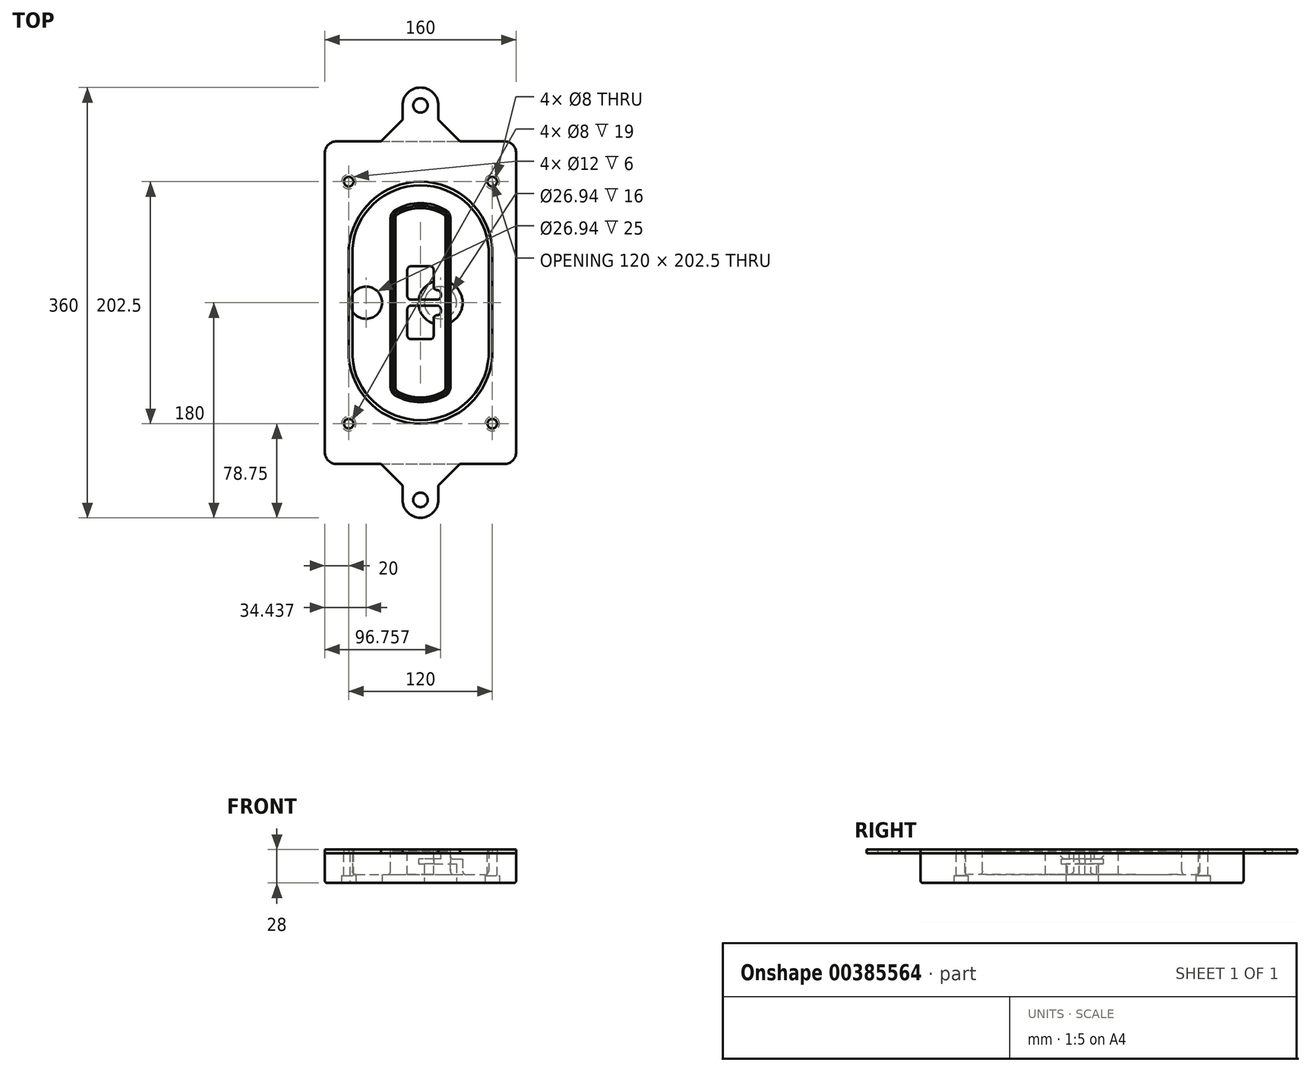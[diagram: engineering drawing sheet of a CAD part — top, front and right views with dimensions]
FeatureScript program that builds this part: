
annotation { "Feature Type Name" : "Feature", "Feature Type Description" : "" }
export const myFeature = defineFeature(function(context is Context, id is Id, definition is map)
    precondition{}
    {
        {
            var Q0;
            Q0=qCreatedBy(makeId("Top.planeOp"),FACE);
            var sketch = newSketch(context, id + "F0", { "sketchPlane" : qUnion([Q0])});
            skPoint(sketch, "E0.rect.middle", {"position": v(0, 0) * mm});
            skLineSegment(sketch, "E1.bottom", {"start": v(-70, -135) * mm, "end": v(70, -135) * mm});
            skLineSegment(sketch, "E1.top", {"start": v(-70, 135) * mm, "end": v(70, 135) * mm});
            skLineSegment(sketch, "E1.left", {"start": v(-80, -125) * mm, "end": v(-80, 125) * mm});
            skLineSegment(sketch, "E1.right", {"start": v(80, -125) * mm, "end": v(80, 125) * mm});
            skLineSegment(sketch, "E2", {"start": v(-80, 135) * mm, "end": v(80, -135) * mm, "construction": true});
            skLineSegment(sketch, "E3", {"start": v(80, 135) * mm, "end": v(-80, -135) * mm, "construction": true});
            skCircle(sketch, "E4", {"center": v(-60, 101.25) * mm, "radius": 4 * mm});
            skCircle(sketch, "E5", {"center": v(60, 101.25) * mm, "radius": 4 * mm});
            skCircle(sketch, "E6", {"center": v(60, -101.25) * mm, "radius": 4 * mm});
            skCircle(sketch, "E7", {"center": v(-60, -101.25) * mm, "radius": 4 * mm});
            skLineSegment(sketch, "E8", {"start": v(-60, 101.25) * mm, "end": v(60, 101.25) * mm, "construction": true});
            skLineSegment(sketch, "E9", {"start": v(60, 101.25) * mm, "end": v(60, -101.25) * mm, "construction": true});
            skLineSegment(sketch, "E10", {"start": v(60, -101.25) * mm, "end": v(-60, -101.25) * mm, "construction": true});
            skLineSegment(sketch, "E11", {"start": v(-60, -101.25) * mm, "end": v(-60, 101.25) * mm, "construction": true});
            skLineSegment(sketch, "E12", {"start": v(-60, 44.66) * mm, "end": v(-60, -44.66) * mm});
            skLineSegment(sketch, "E13", {"start": v(60, 44.66) * mm, "end": v(60, -44.66) * mm});
            skArc(sketch, "E14", {"start": v(59.98, 45.37) * mm, "mid": v(0, 101.25) * mm, "end": v(-59.98, 45.37) * mm});
            skArc(sketch, "E15", {"start": v(-59.98, -45.37) * mm, "mid": v(0, -101.25) * mm, "end": v(59.98, -45.37) * mm});
            skLineSegment(sketch, "E16", {"start": v(-60, 0) * mm, "end": v(60, 0) * mm, "construction": true});
            skPoint(sketch, "E17.visualSharp", {"position": v(-60, -45) * mm});
            skArc(sketch, "E17.filletArc", {"start": v(-60, -44.66) * mm, "mid": v(-60, -45.02) * mm, "end": v(-59.98, -45.37) * mm});
            skPoint(sketch, "E18.visualSharp", {"position": v(-60, 45) * mm});
            skArc(sketch, "E18.filletArc", {"start": v(-59.98, 45.37) * mm, "mid": v(-60, 45.02) * mm, "end": v(-60, 44.66) * mm});
            skPoint(sketch, "E19.visualSharp", {"position": v(60, 45) * mm});
            skArc(sketch, "E19.filletArc", {"start": v(60, 44.66) * mm, "mid": v(60, 45.02) * mm, "end": v(59.98, 45.37) * mm});
            skPoint(sketch, "E20.visualSharp", {"position": v(60, -45) * mm});
            skArc(sketch, "E20.filletArc", {"start": v(59.98, -45.37) * mm, "mid": v(60, -45.02) * mm, "end": v(60, -44.66) * mm});
            skPoint(sketch, "E21.visualSharp", {"position": v(-80, 135) * mm});
            skArc(sketch, "E21.filletArc", {"start": v(-70, 135) * mm, "mid": v(-77.07, 132.07) * mm, "end": v(-80, 125) * mm});
            skPoint(sketch, "E22.visualSharp", {"position": v(80, 135) * mm});
            skArc(sketch, "E22.filletArc", {"start": v(80, 125) * mm, "mid": v(77.07, 132.07) * mm, "end": v(70, 135) * mm});
            skPoint(sketch, "E23.visualSharp", {"position": v(80, -135) * mm});
            skArc(sketch, "E23.filletArc", {"start": v(70, -135) * mm, "mid": v(77.07, -132.07) * mm, "end": v(80, -125) * mm});
            skPoint(sketch, "E24.visualSharp", {"position": v(-80, -135) * mm});
            skArc(sketch, "E24.filletArc", {"start": v(-80, -125) * mm, "mid": v(-77.07, -132.07) * mm, "end": v(-70, -135) * mm});
            skArc(sketch, "E25.0", {"start": v(57, 44.66) * mm, "mid": v(57, 44.9) * mm, "end": v(56.98, 45.16) * mm});
            skLineSegment(sketch, "E25.1", {"start": v(57, 44.66) * mm, "end": v(57, -44.66) * mm});
            skArc(sketch, "E25.2", {"start": v(56.98, -45.16) * mm, "mid": v(57, -44.9) * mm, "end": v(57, -44.66) * mm});
            skArc(sketch, "E25.3", {"start": v(-56.98, -45.16) * mm, "mid": v(0, -98.25) * mm, "end": v(56.98, -45.16) * mm});
            skArc(sketch, "E25.4", {"start": v(-57, -44.66) * mm, "mid": v(-57, -44.9) * mm, "end": v(-56.98, -45.16) * mm});
            skArc(sketch, "E25.5", {"start": v(56.98, 45.16) * mm, "mid": v(0, 98.25) * mm, "end": v(-56.98, 45.16) * mm});
            skLineSegment(sketch, "E25.6", {"start": v(-57, 44.66) * mm, "end": v(-57, -44.66) * mm});
            skArc(sketch, "E25.7", {"start": v(-56.98, 45.16) * mm, "mid": v(-57, 44.9) * mm, "end": v(-57, 44.66) * mm});
            skArc(sketch, "E26.0", {"start": v(-63.97, 45.65) * mm, "mid": v(-64, 45.16) * mm, "end": v(-64, 44.66) * mm});
            skArc(sketch, "E26.1", {"start": v(63.97, 45.65) * mm, "mid": v(0, 105.25) * mm, "end": v(-63.97, 45.65) * mm});
            skArc(sketch, "E26.2", {"start": v(64, 44.66) * mm, "mid": v(64, 45.16) * mm, "end": v(63.97, 45.65) * mm});
            skLineSegment(sketch, "E26.3", {"start": v(64, 44.66) * mm, "end": v(64, -44.66) * mm});
            skArc(sketch, "E26.4", {"start": v(63.97, -45.65) * mm, "mid": v(64, -45.16) * mm, "end": v(64, -44.66) * mm});
            skLineSegment(sketch, "E26.5", {"start": v(-64, 44.66) * mm, "end": v(-64, -44.66) * mm});
            skArc(sketch, "E26.6", {"start": v(-63.97, -45.65) * mm, "mid": v(0, -105.25) * mm, "end": v(63.97, -45.65) * mm});
            skArc(sketch, "E26.7", {"start": v(-64, -44.66) * mm, "mid": v(-64, -45.16) * mm, "end": v(-63.97, -45.65) * mm});
            skSolve(sketch);
        }
        {
            var Q0;
            Q0=makeQuery(id+"F0.imprint","IMPRINT",FACE,{"disambiguationData":[TD([[makeQuery(id+"F0.imprint","IMPRINT",EDGE,{"derivedFrom":sQuery(id+"F0.wireOp",EDGE,"E1.bottom")}),1.0]])]});
            var Q1;
            Q1=makeQuery(id+"F0.imprint","IMPRINT",FACE,{"disambiguationData":[TD([[makeQuery(id+"F0.imprint","IMPRINT",EDGE,{"derivedFrom":sQuery(id+"F0.wireOp",EDGE,"E12")}),1.0]])]});
            var Q2;
            Q2=makeQuery(id+"F0.imprint","IMPRINT",FACE,{"disambiguationData":[TD([[makeQuery(id+"F0.imprint","IMPRINT",EDGE,{"derivedFrom":sQuery(id+"F0.wireOp",EDGE,"E25.0")}),1.0]])]});
            var Q3;
            Q3=makeQuery(id+"F0.imprint","IMPRINT",FACE,{"disambiguationData":[TD([[makeQuery(id+"F0.imprint","IMPRINT",EDGE,{"derivedFrom":sQuery(id+"F0.wireOp",EDGE,"E12")}),-1.0]])]});
            extrude(context, id + "F1", {"entities" : qUnion([Q0, Q1, Q2, Q3]), "oppositeDirection" : true, "depth" : 25 * mm});
        }
        {
            var Q0;
            Q0=makeQuery(id+"F0.imprint","IMPRINT",FACE,{"disambiguationData":[TD([[makeQuery(id+"F0.imprint","IMPRINT",EDGE,{"derivedFrom":sQuery(id+"F0.wireOp",EDGE,"E12")}),1.0]])]});
            extrude(context, id + "F2", {"entities" : qUnion([Q0]), "operationType" : NewBodyOperationType.ADD, "depth" : 3 * mm});
        }
        {
            var Q0;
            Q0=makeQuery(id+"F0.imprint","IMPRINT",FACE,{"disambiguationData":[TD([[makeQuery(id+"F0.imprint","IMPRINT",EDGE,{"derivedFrom":sQuery(id+"F0.wireOp",EDGE,"E25.0")}),1.0]])]});
            extrude(context, id + "F3", {"entities" : qUnion([Q0]), "operationType" : NewBodyOperationType.REMOVE, "oppositeDirection" : true, "depth" : 18 * mm});
        }
        {
            var Q0;
            Q0=makeQuery(id+"F2.opExtrude","CAP_FACE",FACE,{"disambiguationData":[OSD([sQuery(id+"F0.wireOp",EDGE,"E12"),sQuery(id+"F0.wireOp",EDGE,"E13"),sQuery(id+"F0.wireOp",EDGE,"E14"),sQuery(id+"F0.wireOp",EDGE,"E15"),sQuery(id+"F0.wireOp",EDGE,"E17.filletArc"),sQuery(id+"F0.wireOp",EDGE,"E18.filletArc"),sQuery(id+"F0.wireOp",EDGE,"E19.filletArc"),sQuery(id+"F0.wireOp",EDGE,"E20.filletArc"),sQuery(id+"F0.wireOp",EDGE,"E25.0"),sQuery(id+"F0.wireOp",EDGE,"E25.1"),sQuery(id+"F0.wireOp",EDGE,"E25.2"),sQuery(id+"F0.wireOp",EDGE,"E25.3"),sQuery(id+"F0.wireOp",EDGE,"E25.4"),sQuery(id+"F0.wireOp",EDGE,"E25.5"),sQuery(id+"F0.wireOp",EDGE,"E25.6"),sQuery(id+"F0.wireOp",EDGE,"E25.7")])],"isStart":false});
            var sketch = newSketch(context, id + "F4", { "sketchPlane" : qUnion([Q0])});
            skArc(sketch, "E27.0", {"start": v(-20.99, -77.65) * mm, "mid": v(0, -83.25) * mm, "end": v(20.99, -77.65) * mm});
            skArc(sketch, "E28.0", {"start": v(20.99, 77.65) * mm, "mid": v(0, 83.25) * mm, "end": v(-20.99, 77.65) * mm});
            skLineSegment(sketch, "E29", {"start": v(-25, 70.71) * mm, "end": v(-25, -70.71) * mm});
            skLineSegment(sketch, "E30", {"start": v(25, 70.71) * mm, "end": v(25, -70.71) * mm});
            skLineSegment(sketch, "E31", {"start": v(-25, 75.03) * mm, "end": v(25, 75.03) * mm, "construction": true});
            skLineSegment(sketch, "E32", {"start": v(-25, -75.03) * mm, "end": v(25, -75.03) * mm, "construction": true});
            skPoint(sketch, "E33.visualSharp", {"position": v(-25, 75.03) * mm});
            skArc(sketch, "E33.filletArc", {"start": v(-20.99, 77.65) * mm, "mid": v(-23.92, 74.72) * mm, "end": v(-25, 70.71) * mm});
            skPoint(sketch, "E34.visualSharp", {"position": v(25, 75.03) * mm});
            skArc(sketch, "E34.filletArc", {"start": v(25, 70.71) * mm, "mid": v(23.92, 74.72) * mm, "end": v(20.99, 77.65) * mm});
            skPoint(sketch, "E35.visualSharp", {"position": v(25, -75.03) * mm});
            skArc(sketch, "E35.filletArc", {"start": v(20.99, -77.65) * mm, "mid": v(23.92, -74.72) * mm, "end": v(25, -70.71) * mm});
            skPoint(sketch, "E36.visualSharp", {"position": v(-25, -75.03) * mm});
            skArc(sketch, "E36.filletArc", {"start": v(-25, -70.71) * mm, "mid": v(-23.92, -74.72) * mm, "end": v(-20.99, -77.65) * mm});
            skArc(sketch, "E37.0", {"start": v(56.98, 45.16) * mm, "mid": v(0, 98.25) * mm, "end": v(-56.98, 45.16) * mm});
            skArc(sketch, "E37.1", {"start": v(-56.98, 45.16) * mm, "mid": v(-57, 44.9) * mm, "end": v(-57, 44.66) * mm});
            skLineSegment(sketch, "E37.2", {"start": v(-57, 44.66) * mm, "end": v(-57, -44.66) * mm});
            skArc(sketch, "E37.3", {"start": v(-57, -44.66) * mm, "mid": v(-57, -44.9) * mm, "end": v(-56.98, -45.16) * mm});
            skArc(sketch, "E37.4", {"start": v(-56.98, -45.16) * mm, "mid": v(0, -98.25) * mm, "end": v(56.98, -45.16) * mm});
            skArc(sketch, "E37.5", {"start": v(56.98, -45.16) * mm, "mid": v(57, -44.9) * mm, "end": v(57, -44.66) * mm});
            skLineSegment(sketch, "E37.6", {"start": v(57, 44.66) * mm, "end": v(57, -44.66) * mm});
            skArc(sketch, "E37.7", {"start": v(57, 44.66) * mm, "mid": v(57, 44.9) * mm, "end": v(56.98, 45.16) * mm});
            skLineSegment(sketch, "E38.0", {"start": v(23, 70.71) * mm, "end": v(23, -70.71) * mm});
            skArc(sketch, "E38.1", {"start": v(19.99, -75.92) * mm, "mid": v(22.2, -73.72) * mm, "end": v(23, -70.71) * mm});
            skArc(sketch, "E38.2", {"start": v(-19.99, -75.92) * mm, "mid": v(0, -81.25) * mm, "end": v(19.99, -75.92) * mm});
            skArc(sketch, "E38.3", {"start": v(-23, -70.71) * mm, "mid": v(-22.2, -73.72) * mm, "end": v(-19.99, -75.92) * mm});
            skLineSegment(sketch, "E38.4", {"start": v(-23, 70.71) * mm, "end": v(-23, -70.71) * mm});
            skArc(sketch, "E38.5", {"start": v(23, 70.71) * mm, "mid": v(22.2, 73.72) * mm, "end": v(19.99, 75.92) * mm});
            skArc(sketch, "E38.6", {"start": v(-19.99, 75.92) * mm, "mid": v(-22.2, 73.72) * mm, "end": v(-23, 70.71) * mm});
            skArc(sketch, "E38.7", {"start": v(19.99, 75.92) * mm, "mid": v(0, 81.25) * mm, "end": v(-19.99, 75.92) * mm});
            skArc(sketch, "E39.0", {"start": v(21, 70.71) * mm, "mid": v(20.46, 72.72) * mm, "end": v(19, 74.18) * mm});
            skLineSegment(sketch, "E39.1", {"start": v(21, 70.71) * mm, "end": v(21, -70.71) * mm});
            skArc(sketch, "E39.2", {"start": v(19, -74.18) * mm, "mid": v(20.46, -72.72) * mm, "end": v(21, -70.71) * mm});
            skArc(sketch, "E39.3", {"start": v(-19, -74.18) * mm, "mid": v(0, -79.25) * mm, "end": v(19, -74.18) * mm});
            skArc(sketch, "E39.4", {"start": v(-21, -70.71) * mm, "mid": v(-20.46, -72.72) * mm, "end": v(-19, -74.18) * mm});
            skArc(sketch, "E39.5", {"start": v(19, 74.18) * mm, "mid": v(0, 79.25) * mm, "end": v(-19, 74.18) * mm});
            skLineSegment(sketch, "E39.6", {"start": v(-21, 70.71) * mm, "end": v(-21, -70.71) * mm});
            skArc(sketch, "E39.7", {"start": v(-19, 74.18) * mm, "mid": v(-20.46, 72.72) * mm, "end": v(-21, 70.71) * mm});
            skLineSegment(sketch, "E40", {"start": v(-25, 0) * mm, "end": v(25, 0) * mm, "construction": true});
            skLineSegment(sketch, "E41", {"start": v(-11, 5.5) * mm, "end": v(-11, 27.5) * mm});
            skLineSegment(sketch, "E42", {"start": v(-8, 30.5) * mm, "end": v(8, 30.5) * mm});
            skLineSegment(sketch, "E43", {"start": v(11, 27.5) * mm, "end": v(11, 13.5) * mm});
            skLineSegment(sketch, "E44", {"start": v(14, 10.5) * mm, "end": v(14, 10.5) * mm});
            skLineSegment(sketch, "E45", {"start": v(17, 7.5) * mm, "end": v(17, 5.5) * mm});
            skLineSegment(sketch, "E46", {"start": v(14, 2.5) * mm, "end": v(-8, 2.5) * mm});
            skPoint(sketch, "E47.visualSharp", {"position": v(-11, 30.5) * mm});
            skArc(sketch, "E47.filletArc", {"start": v(-8, 30.5) * mm, "mid": v(-10.12, 29.62) * mm, "end": v(-11, 27.5) * mm});
            skPoint(sketch, "E48.visualSharp", {"position": v(11, 30.5) * mm});
            skArc(sketch, "E48.filletArc", {"start": v(11, 27.5) * mm, "mid": v(10.12, 29.62) * mm, "end": v(8, 30.5) * mm});
            skPoint(sketch, "E49.visualSharp", {"position": v(11, 10.5) * mm});
            skArc(sketch, "E49.filletArc", {"start": v(11, 13.5) * mm, "mid": v(11.88, 11.38) * mm, "end": v(14, 10.5) * mm});
            skPoint(sketch, "E50.visualSharp", {"position": v(17, 10.5) * mm});
            skArc(sketch, "E50.filletArc", {"start": v(17, 7.5) * mm, "mid": v(16.12, 9.62) * mm, "end": v(14, 10.5) * mm});
            skPoint(sketch, "E51.visualSharp", {"position": v(17, 2.5) * mm});
            skArc(sketch, "E51.filletArc", {"start": v(14, 2.5) * mm, "mid": v(16.12, 3.38) * mm, "end": v(17, 5.5) * mm});
            skPoint(sketch, "E52.visualSharp", {"position": v(-11, 2.5) * mm});
            skArc(sketch, "E52.filletArc", {"start": v(-11, 5.5) * mm, "mid": v(-10.12, 3.38) * mm, "end": v(-8, 2.5) * mm});
            skLineSegment(sketch, "E53.0.MirrorCS", {"start": v(14, -2.5) * mm, "end": v(-8, -2.5) * mm});
            skArc(sketch, "E54.0.MirrorCS", {"start": v(-11, -5.5) * mm, "mid": v(-10.12, -3.38) * mm, "end": v(-8, -2.5) * mm});
            skLineSegment(sketch, "E55.0.MirrorCS", {"start": v(-11, -5.5) * mm, "end": v(-11, -27.5) * mm});
            skArc(sketch, "E56.0.MirrorCS", {"start": v(-8, -30.5) * mm, "mid": v(-10.12, -29.62) * mm, "end": v(-11, -27.5) * mm});
            skLineSegment(sketch, "E57.0.MirrorCS", {"start": v(-8, -30.5) * mm, "end": v(8, -30.5) * mm});
            skArc(sketch, "E58.0.MirrorCS", {"start": v(11, -27.5) * mm, "mid": v(10.12, -29.62) * mm, "end": v(8, -30.5) * mm});
            skLineSegment(sketch, "E59.0.MirrorCS", {"start": v(11, -27.5) * mm, "end": v(11, -13.5) * mm});
            skArc(sketch, "E60.0.MirrorCS", {"start": v(11, -13.5) * mm, "mid": v(11.88, -11.38) * mm, "end": v(14, -10.5) * mm});
            skArc(sketch, "E61.0.MirrorCS", {"start": v(17, -7.5) * mm, "mid": v(16.12, -9.62) * mm, "end": v(14, -10.5) * mm});
            skLineSegment(sketch, "E62.0.MirrorCS", {"start": v(17, -7.5) * mm, "end": v(17, -5.5) * mm});
            skArc(sketch, "E63.0.MirrorCS", {"start": v(14, -2.5) * mm, "mid": v(16.12, -3.38) * mm, "end": v(17, -5.5) * mm});
            skSolve(sketch);
        }
        {
            var Q0;
            Q0=makeQuery(id+"F4.imprint","IMPRINT",FACE,{"disambiguationData":[TD([[makeQuery(id+"F4.imprint","IMPRINT",EDGE,{"derivedFrom":sQuery(id+"F4.wireOp",EDGE,"E27.0")}),1.0]])]});
            var Q1;
            Q1=makeQuery(id+"F4.imprint","IMPRINT",FACE,{"disambiguationData":[TD([[makeQuery(id+"F4.imprint","IMPRINT",EDGE,{"derivedFrom":sQuery(id+"F4.wireOp",EDGE,"E38.0")}),-1.0]])]});
            var Q2;
            Q2=makeQuery(id+"F4.imprint","IMPRINT",FACE,{"disambiguationData":[TD([[makeQuery(id+"F4.imprint","IMPRINT",EDGE,{"derivedFrom":sQuery(id+"F4.wireOp",EDGE,"E39.0")}),1.0]])]});
            extrude(context, id + "F5", {"entities" : qUnion([Q0, Q1, Q2]), "operationType" : NewBodyOperationType.ADD, "endBound" : BoundingType.UP_TO_NEXT, "oppositeDirection" : true, "depth" : 25 * mm});
        }
        {
            var Q0;
            Q0=makeQuery(id+"F4.imprint","IMPRINT",FACE,{"disambiguationData":[TD([[makeQuery(id+"F4.imprint","IMPRINT",EDGE,{"derivedFrom":sQuery(id+"F4.wireOp",EDGE,"E38.0")}),-1.0]])]});
            extrude(context, id + "F6", {"entities" : qUnion([Q0]), "operationType" : NewBodyOperationType.REMOVE, "oppositeDirection" : true, "depth" : 2 * mm});
        }
        {
            var Q0;
            Q0=makeQuery(id+"F1.opExtrude","CAP_FACE",FACE,{"disambiguationData":[OSD([sQuery(id+"F0.wireOp",EDGE,"E1.bottom"),sQuery(id+"F0.wireOp",EDGE,"E1.top"),sQuery(id+"F0.wireOp",EDGE,"E1.left"),sQuery(id+"F0.wireOp",EDGE,"E1.right"),sQuery(id+"F0.wireOp",EDGE,"E4"),sQuery(id+"F0.wireOp",EDGE,"E5"),sQuery(id+"F0.wireOp",EDGE,"E6"),sQuery(id+"F0.wireOp",EDGE,"E7"),sQuery(id+"F0.wireOp",EDGE,"E21.filletArc"),sQuery(id+"F0.wireOp",EDGE,"E22.filletArc"),sQuery(id+"F0.wireOp",EDGE,"E23.filletArc"),sQuery(id+"F0.wireOp",EDGE,"E24.filletArc")])],"isStart":false});
            var sketch = newSketch(context, id + "F7", { "sketchPlane" : qUnion([Q0])});
            skCircle(sketch, "E64", {"center": v(16.76, 0) * mm, "radius": 13.47 * mm});
            skCircle(sketch, "E65", {"center": v(-45.56, 0) * mm, "radius": 13.47 * mm});
            skLineSegment(sketch, "E66", {"start": v(80, 0) * mm, "end": v(-80, 0) * mm});
            skCircle(sketch, "E67", {"center": v(16.76, 0) * mm, "radius": 18.47 * mm});
            skCircle(sketch, "E68", {"center": v(60, -101.25) * mm, "radius": 6 * mm});
            skCircle(sketch, "E69", {"center": v(-60, -101.25) * mm, "radius": 6 * mm});
            skCircle(sketch, "E70", {"center": v(-60, 101.25) * mm, "radius": 6 * mm});
            skCircle(sketch, "E71", {"center": v(60, 101.25) * mm, "radius": 6 * mm});
            skSolve(sketch);
        }
        {
            var Q0;
            {var subQ1=sQuery(id+"F7.wireOp",EDGE,"E66");var subQ4=sQuery(id+"F7.wireOp",EDGE,"E64");var subQ6=makeQuery(id+"F7.imprint","INTERSECT",VERTEX,{"disambiguationData":[OD(0.0)],"derivedFrom":[subQ4,subQ1]});Q0=makeQuery(id+"F7.imprint","IMPRINT",FACE,{"disambiguationData":[TD([[makeQuery(id+"F7.imprint","IMPRINT",EDGE,{"disambiguationData":[TD([[subQ6,-1.0]])],"derivedFrom":subQ4}),-1.0]])]});}
            var Q1;
            {var subQ0=sQuery(id+"F7.wireOp",EDGE,"E66");var subQ1=sQuery(id+"F7.wireOp",EDGE,"E64");var subQ3=makeQuery(id+"F7.imprint","INTERSECT",VERTEX,{"disambiguationData":[OD(0.0)],"derivedFrom":[subQ1,subQ0]});Q1=makeQuery(id+"F7.imprint","IMPRINT",FACE,{"disambiguationData":[TD([[makeQuery(id+"F7.imprint","IMPRINT",EDGE,{"disambiguationData":[TD([[subQ3,-1.0]])],"derivedFrom":subQ1}),1.0]])]});}
            var Q2;
            {var subQ0=sQuery(id+"F7.wireOp",EDGE,"E66");var subQ1=sQuery(id+"F7.wireOp",EDGE,"E64");var subQ3=makeQuery(id+"F7.imprint","INTERSECT",VERTEX,{"disambiguationData":[OD(0.0)],"derivedFrom":[subQ1,subQ0]});Q2=makeQuery(id+"F7.imprint","IMPRINT",FACE,{"disambiguationData":[TD([[makeQuery(id+"F7.imprint","IMPRINT",EDGE,{"disambiguationData":[TD([[subQ3,1.0]])],"derivedFrom":subQ1}),1.0]])]});}
            var Q3;
            {var subQ1=sQuery(id+"F7.wireOp",EDGE,"E66");var subQ4=sQuery(id+"F7.wireOp",EDGE,"E64");var subQ6=makeQuery(id+"F7.imprint","INTERSECT",VERTEX,{"disambiguationData":[OD(0.0)],"derivedFrom":[subQ4,subQ1]});Q3=makeQuery(id+"F7.imprint","IMPRINT",FACE,{"disambiguationData":[TD([[makeQuery(id+"F7.imprint","IMPRINT",EDGE,{"disambiguationData":[TD([[subQ6,1.0]])],"derivedFrom":subQ4}),-1.0]])]});}
            extrude(context, id + "F8", {"entities" : qUnion([Q0, Q1, Q2, Q3]), "operationType" : NewBodyOperationType.ADD, "oppositeDirection" : true, "depth" : 20 * mm});
        }
        {
            var Q0;
            {var subQ0=sQuery(id+"F7.wireOp",EDGE,"E66");var subQ1=sQuery(id+"F7.wireOp",EDGE,"E64");var subQ3=makeQuery(id+"F7.imprint","INTERSECT",VERTEX,{"disambiguationData":[OD(0.0)],"derivedFrom":[subQ1,subQ0]});Q0=makeQuery(id+"F7.imprint","IMPRINT",FACE,{"disambiguationData":[TD([[makeQuery(id+"F7.imprint","IMPRINT",EDGE,{"disambiguationData":[TD([[subQ3,-1.0]])],"derivedFrom":subQ1}),1.0]])]});}
            var Q1;
            {var subQ0=sQuery(id+"F7.wireOp",EDGE,"E66");var subQ1=sQuery(id+"F7.wireOp",EDGE,"E64");var subQ3=makeQuery(id+"F7.imprint","INTERSECT",VERTEX,{"disambiguationData":[OD(0.0)],"derivedFrom":[subQ1,subQ0]});Q1=makeQuery(id+"F7.imprint","IMPRINT",FACE,{"disambiguationData":[TD([[makeQuery(id+"F7.imprint","IMPRINT",EDGE,{"disambiguationData":[TD([[subQ3,1.0]])],"derivedFrom":subQ1}),1.0]])]});}
            extrude(context, id + "F9", {"entities" : qUnion([Q0, Q1]), "operationType" : NewBodyOperationType.REMOVE, "oppositeDirection" : true, "depth" : 16 * mm});
        }
        {
            var Q0;
            {var subQ0=sQuery(id+"F7.wireOp",EDGE,"E66");var subQ1=sQuery(id+"F7.wireOp",EDGE,"E65");var subQ3=makeQuery(id+"F7.imprint","INTERSECT",VERTEX,{"disambiguationData":[OD(0.0)],"derivedFrom":[subQ1,subQ0]});Q0=makeQuery(id+"F7.imprint","IMPRINT",FACE,{"disambiguationData":[TD([[makeQuery(id+"F7.imprint","IMPRINT",EDGE,{"disambiguationData":[TD([[subQ3,-1.0]])],"derivedFrom":subQ1}),1.0]])]});}
            var Q1;
            {var subQ0=sQuery(id+"F7.wireOp",EDGE,"E66");var subQ1=sQuery(id+"F7.wireOp",EDGE,"E65");var subQ3=makeQuery(id+"F7.imprint","INTERSECT",VERTEX,{"disambiguationData":[OD(0.0)],"derivedFrom":[subQ1,subQ0]});Q1=makeQuery(id+"F7.imprint","IMPRINT",FACE,{"disambiguationData":[TD([[makeQuery(id+"F7.imprint","IMPRINT",EDGE,{"disambiguationData":[TD([[subQ3,1.0]])],"derivedFrom":subQ1}),1.0]])]});}
            extrude(context, id + "F10", {"entities" : qUnion([Q0, Q1]), "operationType" : NewBodyOperationType.REMOVE, "oppositeDirection" : true, "depth" : 25 * mm});
        }
        {
            var Q0;
            Q0=makeQuery(id+"F7.imprint","IMPRINT",FACE,{"disambiguationData":[TD([[makeQuery(id+"F7.imprint","IMPRINT",EDGE,{"derivedFrom":sQuery(id+"F7.wireOp",EDGE,"E68")}),1.0]])]});
            var Q1;
            Q1=makeQuery(id+"F7.imprint","IMPRINT",FACE,{"disambiguationData":[TD([[makeQuery(id+"F7.imprint","IMPRINT",EDGE,{"derivedFrom":makeQuery(id+"F1.opExtrude","CAP_EDGE",EDGE,{"disambiguationData":[OSD([sQuery(id+"F0.wireOp",EDGE,"E5")])],"isStart":false})}),-1.0]])]});
            var Q2;
            Q2=makeQuery(id+"F7.imprint","IMPRINT",FACE,{"disambiguationData":[TD([[makeQuery(id+"F7.imprint","IMPRINT",EDGE,{"derivedFrom":sQuery(id+"F7.wireOp",EDGE,"E69")}),1.0]])]});
            var Q3;
            Q3=makeQuery(id+"F7.imprint","IMPRINT",FACE,{"disambiguationData":[TD([[makeQuery(id+"F7.imprint","IMPRINT",EDGE,{"derivedFrom":makeQuery(id+"F1.opExtrude","CAP_EDGE",EDGE,{"disambiguationData":[OSD([sQuery(id+"F0.wireOp",EDGE,"E4")])],"isStart":false})}),-1.0]])]});
            var Q4;
            Q4=makeQuery(id+"F7.imprint","IMPRINT",FACE,{"disambiguationData":[TD([[makeQuery(id+"F7.imprint","IMPRINT",EDGE,{"derivedFrom":sQuery(id+"F7.wireOp",EDGE,"E70")}),1.0]])]});
            var Q5;
            Q5=makeQuery(id+"F7.imprint","IMPRINT",FACE,{"disambiguationData":[TD([[makeQuery(id+"F7.imprint","IMPRINT",EDGE,{"derivedFrom":makeQuery(id+"F1.opExtrude","CAP_EDGE",EDGE,{"disambiguationData":[OSD([sQuery(id+"F0.wireOp",EDGE,"E7")])],"isStart":false})}),-1.0]])]});
            var Q6;
            Q6=makeQuery(id+"F7.imprint","IMPRINT",FACE,{"disambiguationData":[TD([[makeQuery(id+"F7.imprint","IMPRINT",EDGE,{"derivedFrom":sQuery(id+"F7.wireOp",EDGE,"E71")}),1.0]])]});
            var Q7;
            Q7=makeQuery(id+"F7.imprint","IMPRINT",FACE,{"disambiguationData":[TD([[makeQuery(id+"F7.imprint","IMPRINT",EDGE,{"derivedFrom":makeQuery(id+"F1.opExtrude","CAP_EDGE",EDGE,{"disambiguationData":[OSD([sQuery(id+"F0.wireOp",EDGE,"E6")])],"isStart":false})}),-1.0]])]});
            extrude(context, id + "F11", {"entities" : qUnion([Q0, Q1, Q2, Q3, Q4, Q5, Q6, Q7]), "operationType" : NewBodyOperationType.REMOVE, "oppositeDirection" : true, "depth" : 6 * mm});
        }
        {
            var Q0;
            Q0=makeQuery(id+"F9.boolean.opBoolean","COPY",FACE,{"derivedFrom":makeQuery(id+"F9.opExtrude","CAP_FACE",FACE,{"disambiguationData":[OSD([sQuery(id+"F7.wireOp",EDGE,"E64")])],"isStart":false})});
            var sketch = newSketch(context, id + "F12", { "sketchPlane" : qUnion([Q0])});
            skArc(sketch, "E72.0", {"start": v(11, 17.55) * mm, "mid": v(2.57, 11.82) * mm, "end": v(-1.54, 2.5) * mm});
            skArc(sketch, "E72.1", {"start": v(-1.54, -2.5) * mm, "mid": v(2.57, -11.82) * mm, "end": v(11, -17.55) * mm});
            skLineSegment(sketch, "E73", {"start": v(-1.54, -2.5) * mm, "end": v(14, -2.5) * mm});
            skLineSegment(sketch, "E74.0", {"start": v(14, 2.5) * mm, "end": v(-1.54, 2.5) * mm});
            skArc(sketch, "E74.1", {"start": v(14, 2.5) * mm, "mid": v(16.12, 3.38) * mm, "end": v(17, 5.5) * mm});
            skLineSegment(sketch, "E74.2", {"start": v(17, 7.5) * mm, "end": v(17, 5.5) * mm});
            skArc(sketch, "E74.3", {"start": v(17, 7.5) * mm, "mid": v(16.12, 9.62) * mm, "end": v(14, 10.5) * mm});
            skArc(sketch, "E74.4", {"start": v(11, 13.5) * mm, "mid": v(11.88, 11.38) * mm, "end": v(14, 10.5) * mm});
            skLineSegment(sketch, "E74.5", {"start": v(11, 17.55) * mm, "end": v(11, 13.5) * mm});
            skLineSegment(sketch, "E74.7", {"start": v(14, -2.5) * mm, "end": v(-1.54, -2.5) * mm});
            skArc(sketch, "E74.8", {"start": v(14, -2.5) * mm, "mid": v(16.12, -3.38) * mm, "end": v(17, -5.5) * mm});
            skLineSegment(sketch, "E74.9", {"start": v(17, -7.5) * mm, "end": v(17, -5.5) * mm});
            skArc(sketch, "E74.10", {"start": v(17, -7.5) * mm, "mid": v(16.12, -9.62) * mm, "end": v(14, -10.5) * mm});
            skArc(sketch, "E74.11", {"start": v(11, -13.5) * mm, "mid": v(11.88, -11.38) * mm, "end": v(14, -10.5) * mm});
            skLineSegment(sketch, "E74.12", {"start": v(11, -17.55) * mm, "end": v(11, -13.5) * mm});
            skPoint(sketch, "E75.orphan", {"position": v(11, -27.5) * mm});
            skPoint(sketch, "E76.orphan", {"position": v(-8, -2.5) * mm});
            skPoint(sketch, "E77.orphan", {"position": v(-8, 2.5) * mm});
            skPoint(sketch, "E78.orphan", {"position": v(11, 27.5) * mm});
            skSolve(sketch);
        }
        {
            var Q0;
            {var subQ7=sQuery(id+"F12.wireOp",EDGE,"E72.0");var subQ14=sQuery(id+"F12.wireOp",EDGE,"E72.1");var subQ16=sQuery(id+"F12.wireOp",EDGE,"E74.1");var subQ18=sQuery(id+"F12.wireOp",EDGE,"E74.8");Q0=qUnion([makeQuery(id+"F12.imprint","IMPRINT",FACE,{"disambiguationData":[TD([[makeQuery(id+"F12.imprint","IMPRINT",EDGE,{"derivedFrom":subQ7}),1.0]])]}),makeQuery(id+"F12.imprint","IMPRINT",FACE,{"disambiguationData":[TD([[makeQuery(id+"F12.imprint","IMPRINT",EDGE,{"derivedFrom":subQ14}),1.0]])]}),makeQuery(id+"F12.imprint","IMPRINT",FACE,{"disambiguationData":[TD([[makeQuery(id+"F12.imprint","IMPRINT",EDGE,{"derivedFrom":subQ16}),1.0]])]}),makeQuery(id+"F12.imprint","IMPRINT",FACE,{"disambiguationData":[TD([[makeQuery(id+"F12.imprint","IMPRINT",EDGE,{"derivedFrom":subQ18}),-1.0]])]})]);}
            var Q1;
            Q1=makeQuery(id+"F5.boolean.opBoolean","SPLIT",FACE,{"disambiguationData":[TD([makeQuery(id+"F5.opExtrude","SWEPT_FACE",FACE,{"disambiguationData":[OSD([sQuery(id+"F4.wireOp",EDGE,"E41")])]})])],"derivedFrom":makeQuery(id+"F3.boolean.opBoolean","COPY",FACE,{"derivedFrom":makeQuery(id+"F3.opExtrude","CAP_FACE",FACE,{"disambiguationData":[OSD([sQuery(id+"F0.wireOp",EDGE,"E25.0"),sQuery(id+"F0.wireOp",EDGE,"E25.1"),sQuery(id+"F0.wireOp",EDGE,"E25.2"),sQuery(id+"F0.wireOp",EDGE,"E25.3"),sQuery(id+"F0.wireOp",EDGE,"E25.4"),sQuery(id+"F0.wireOp",EDGE,"E25.5"),sQuery(id+"F0.wireOp",EDGE,"E25.6"),sQuery(id+"F0.wireOp",EDGE,"E25.7")])],"isStart":false})})});
            extrude(context, id + "F13", {"entities" : qUnion([Q0]), "operationType" : NewBodyOperationType.REMOVE, "endBound" : BoundingType.UP_TO_SURFACE, "endBoundEntityFace" : qUnion([Q1]), "depth" : 25 * mm});
        }
        {
            var Q0;
            Q0=makeQuery(id+"F3.boolean.opBoolean","COPY",EDGE,{"derivedFrom":makeQuery(id+"F3.opExtrude","CAP_EDGE",EDGE,{"disambiguationData":[OSD([sQuery(id+"F0.wireOp",EDGE,"E25.6")])],"isStart":false})});
            var Q1;
            Q1=makeQuery(id+"F8.boolean.opBoolean","INTERSECT",EDGE,{"derivedFrom":[makeQuery(id+"F5.opExtrude","SWEPT_FACE",FACE,{"disambiguationData":[OSD([sQuery(id+"F4.wireOp",EDGE,"E30")])]}),makeQuery(id+"F8.opExtrude","CAP_FACE",FACE,{"disambiguationData":[OSD([sQuery(id+"F7.wireOp",EDGE,"E67")])],"isStart":false})]});
            var Q2;
            Q2=makeQuery(id+"F8.boolean.opBoolean","INTERSECT",EDGE,{"disambiguationData":[OD(1.0)],"derivedFrom":[makeQuery(id+"F5.opExtrude","SWEPT_FACE",FACE,{"disambiguationData":[OSD([sQuery(id+"F4.wireOp",EDGE,"E30")])]}),makeQuery(id+"F8.opExtrude","SWEPT_FACE",FACE,{"disambiguationData":[OSD([sQuery(id+"F7.wireOp",EDGE,"E67")])]})]});
            var Q3;
            {var subQ0=sQuery(id+"F4.wireOp",EDGE,"E30");Q3=makeQuery(id+"F8.boolean.opBoolean","SPLIT",EDGE,{"disambiguationData":[TD([makeQuery(id+"F5.opExtrude","SWEPT_FACE",FACE,{"disambiguationData":[OSD([sQuery(id+"F4.wireOp",EDGE,"E35.filletArc")])]})])],"derivedFrom":makeQuery(id+"F5.opExtrude","CAP_EDGE",EDGE,{"disambiguationData":[OSD([subQ0])],"isStart":false})});}
            var Q4;
            {var subQ0=sQuery(id+"F0.wireOp",EDGE,"E25.7");var subQ1=sQuery(id+"F0.wireOp",EDGE,"E25.1");var subQ2=sQuery(id+"F0.wireOp",EDGE,"E25.6");var subQ3=sQuery(id+"F0.wireOp",EDGE,"E25.5");var subQ4=sQuery(id+"F0.wireOp",EDGE,"E25.4");var subQ5=sQuery(id+"F0.wireOp",EDGE,"E25.0");var subQ6=sQuery(id+"F0.wireOp",EDGE,"E25.2");var subQ7=sQuery(id+"F0.wireOp",EDGE,"E25.3");Q4=makeQuery(id+"F8.boolean.opBoolean","INTERSECT",EDGE,{"derivedFrom":[makeQuery(id+"F5.boolean.opBoolean","SPLIT",FACE,{"disambiguationData":[TD([makeQuery(id+"F2.opExtrude","SWEPT_FACE",FACE,{"disambiguationData":[OSD([subQ5])]})])],"derivedFrom":makeQuery(id+"F3.boolean.opBoolean","COPY",FACE,{"derivedFrom":makeQuery(id+"F3.opExtrude","CAP_FACE",FACE,{"disambiguationData":[OSD([subQ5,subQ1,subQ6,subQ7,subQ4,subQ3,subQ2,subQ0])],"isStart":false})})}),makeQuery(id+"F8.opExtrude","SWEPT_FACE",FACE,{"disambiguationData":[OSD([sQuery(id+"F7.wireOp",EDGE,"E67")])]})]});}
            var Q5;
            Q5=makeQuery(id+"F8.boolean.opBoolean","INTERSECT",EDGE,{"disambiguationData":[OD(0.0)],"derivedFrom":[makeQuery(id+"F5.opExtrude","SWEPT_FACE",FACE,{"disambiguationData":[OSD([sQuery(id+"F4.wireOp",EDGE,"E30")])]}),makeQuery(id+"F8.opExtrude","SWEPT_FACE",FACE,{"disambiguationData":[OSD([sQuery(id+"F7.wireOp",EDGE,"E67")])]})]});
            fillet(context, id + "F14", {"entities" : qUnion([Q0, Q1, Q2, Q3, Q4, Q5]), "radius" : 3 * mm, "tangentPropagation" : true, "allowEdgeOverflow" : false});
        }
        {
            var Q0;
            Q0=makeQuery(id+"F1.opExtrude","CAP_EDGE",EDGE,{"disambiguationData":[OSD([sQuery(id+"F0.wireOp",EDGE,"E1.bottom")])],"isStart":false});
            fillet(context, id + "F15", {"entities" : qUnion([Q0]), "radius" : 2 * mm, "tangentPropagation" : true, "allowEdgeOverflow" : false});
        }
        {
            var Q0;
            {var subQ0=sQuery(id+"F0.wireOp",EDGE,"E21.filletArc");var subQ1=sQuery(id+"F0.wireOp",EDGE,"E7");var subQ2=sQuery(id+"F0.wireOp",EDGE,"E6");var subQ3=sQuery(id+"F0.wireOp",EDGE,"E5");var subQ4=sQuery(id+"F0.wireOp",EDGE,"E4");var subQ5=sQuery(id+"F0.wireOp",EDGE,"E22.filletArc");var subQ6=sQuery(id+"F0.wireOp",EDGE,"E1.bottom");var subQ7=sQuery(id+"F0.wireOp",EDGE,"E1.right");var subQ8=sQuery(id+"F0.wireOp",EDGE,"E1.top");var subQ9=sQuery(id+"F0.wireOp",EDGE,"E1.left");var subQ10=sQuery(id+"F0.wireOp",EDGE,"E23.filletArc");var subQ11=sQuery(id+"F0.wireOp",EDGE,"E24.filletArc");Q0=makeQuery(id+"F2.boolean.opBoolean","SPLIT",FACE,{"disambiguationData":[TD([makeQuery(id+"F1.opExtrude","SWEPT_FACE",FACE,{"disambiguationData":[OSD([subQ6])]})])],"derivedFrom":makeQuery(id+"F1.opExtrude","CAP_FACE",FACE,{"disambiguationData":[OSD([subQ6,subQ8,subQ9,subQ7,subQ4,subQ3,subQ2,subQ1,subQ0,subQ5,subQ10,subQ11])],"isStart":true})});}
            var sketch = newSketch(context, id + "F16", { "sketchPlane" : qUnion([Q0])});
            skLineSegment(sketch, "E79.0", {"start": v(-70, 135) * mm, "end": v(70, 135) * mm});
            skArc(sketch, "E79.1", {"start": v(-70, 135) * mm, "mid": v(-77.07, 132.07) * mm, "end": v(-80, 125) * mm});
            skLineSegment(sketch, "E79.2", {"start": v(-80, -125) * mm, "end": v(-80, 125) * mm});
            skArc(sketch, "E79.3", {"start": v(-80, -125) * mm, "mid": v(-77.07, -132.07) * mm, "end": v(-70, -135) * mm});
            skLineSegment(sketch, "E79.4", {"start": v(-70, -135) * mm, "end": v(70, -135) * mm});
            skArc(sketch, "E79.5", {"start": v(70, -135) * mm, "mid": v(77.07, -132.07) * mm, "end": v(80, -125) * mm});
            skLineSegment(sketch, "E79.6", {"start": v(80, -125) * mm, "end": v(80, 125) * mm});
            skArc(sketch, "E79.7", {"start": v(80, 125) * mm, "mid": v(77.07, 132.07) * mm, "end": v(70, 135) * mm});
            skCircle(sketch, "E79.8", {"center": v(60, 101.25) * mm, "radius": 4 * mm});
            skCircle(sketch, "E79.9", {"center": v(-60, 101.25) * mm, "radius": 4 * mm});
            skCircle(sketch, "E79.10", {"center": v(-60, -101.25) * mm, "radius": 4 * mm});
            skCircle(sketch, "E79.11", {"center": v(60, -101.25) * mm, "radius": 4 * mm});
            skArc(sketch, "E80.0", {"start": v(59.98, 45.37) * mm, "mid": v(0, 101.25) * mm, "end": v(-59.98, 45.37) * mm});
            skArc(sketch, "E80.1", {"start": v(-59.98, 45.37) * mm, "mid": v(-60, 45.02) * mm, "end": v(-60, 44.66) * mm});
            skLineSegment(sketch, "E80.2", {"start": v(-60, 44.66) * mm, "end": v(-60, -44.66) * mm});
            skArc(sketch, "E80.3", {"start": v(-60, -44.66) * mm, "mid": v(-60, -45.02) * mm, "end": v(-59.98, -45.37) * mm});
            skArc(sketch, "E80.4", {"start": v(-59.98, -45.37) * mm, "mid": v(0, -101.25) * mm, "end": v(59.98, -45.37) * mm});
            skArc(sketch, "E80.5", {"start": v(59.98, -45.37) * mm, "mid": v(60, -45.02) * mm, "end": v(60, -44.66) * mm});
            skLineSegment(sketch, "E80.6", {"start": v(60, 44.66) * mm, "end": v(60, -44.66) * mm});
            skArc(sketch, "E80.7", {"start": v(60, 44.66) * mm, "mid": v(60, 45.02) * mm, "end": v(59.98, 45.37) * mm});
            skLineSegment(sketch, "E81", {"start": v(0, 135) * mm, "end": v(0, 165) * mm, "construction": true});
            skPoint(sketch, "E81.endSnap0", {"position": v(0, 135) * mm});
            skCircle(sketch, "E82", {"center": v(0, 165) * mm, "radius": 6 * mm});
            skLineSegment(sketch, "E83", {"start": v(-15, 165) * mm, "end": v(-15, 153) * mm});
            skLineSegment(sketch, "E84", {"start": v(15, 165) * mm, "end": v(15, 153) * mm});
            skLineSegment(sketch, "E85", {"start": v(-15, 153) * mm, "end": v(-33, 135) * mm});
            skLineSegment(sketch, "E86", {"start": v(15, 153) * mm, "end": v(33, 135) * mm});
            skArc(sketch, "E87", {"start": v(15, 165) * mm, "mid": v(0, 180) * mm, "end": v(-15, 165) * mm});
            skLineSegment(sketch, "E88", {"start": v(-80, 0) * mm, "end": v(80, 0) * mm, "construction": true});
            skArc(sketch, "E89.MirrorCS", {"start": v(15, -165) * mm, "mid": v(0, -180) * mm, "end": v(-15, -165) * mm});
            skLineSegment(sketch, "E90.MirrorCS", {"start": v(-15, -165) * mm, "end": v(-15, -153) * mm});
            skLineSegment(sketch, "E91.MirrorCS", {"start": v(15, -165) * mm, "end": v(15, -153) * mm});
            skLineSegment(sketch, "E92.MirrorCS", {"start": v(15, -153) * mm, "end": v(33, -135) * mm});
            skLineSegment(sketch, "E93.MirrorCS", {"start": v(-15, -153) * mm, "end": v(-33, -135) * mm});
            skLineSegment(sketch, "E94.MirrorCS", {"start": v(0, -135) * mm, "end": v(0, -165) * mm, "construction": true});
            skCircle(sketch, "E95.MirrorC", {"center": v(0, -165) * mm, "radius": 6 * mm});
            skSolve(sketch);
        }
        {
            var Q0;
            Q0 = qSketchRegion(id + "F16", true);
            var Q1;
            Q1=makeQuery(id+"F2.opExtrude","CAP_FACE",FACE,{"disambiguationData":[OSD([sQuery(id+"F0.wireOp",EDGE,"E12"),sQuery(id+"F0.wireOp",EDGE,"E13"),sQuery(id+"F0.wireOp",EDGE,"E14"),sQuery(id+"F0.wireOp",EDGE,"E15"),sQuery(id+"F0.wireOp",EDGE,"E17.filletArc"),sQuery(id+"F0.wireOp",EDGE,"E18.filletArc"),sQuery(id+"F0.wireOp",EDGE,"E19.filletArc"),sQuery(id+"F0.wireOp",EDGE,"E20.filletArc"),sQuery(id+"F0.wireOp",EDGE,"E25.0"),sQuery(id+"F0.wireOp",EDGE,"E25.1"),sQuery(id+"F0.wireOp",EDGE,"E25.2"),sQuery(id+"F0.wireOp",EDGE,"E25.3"),sQuery(id+"F0.wireOp",EDGE,"E25.4"),sQuery(id+"F0.wireOp",EDGE,"E25.5"),sQuery(id+"F0.wireOp",EDGE,"E25.6"),sQuery(id+"F0.wireOp",EDGE,"E25.7")])],"isStart":false});
            extrude(context, id + "F17", {"entities" : qUnion([Q0]), "endBound" : BoundingType.UP_TO_SURFACE, "endBoundEntityFace" : qUnion([Q1]), "depth" : 25 * mm});
        }
    });
